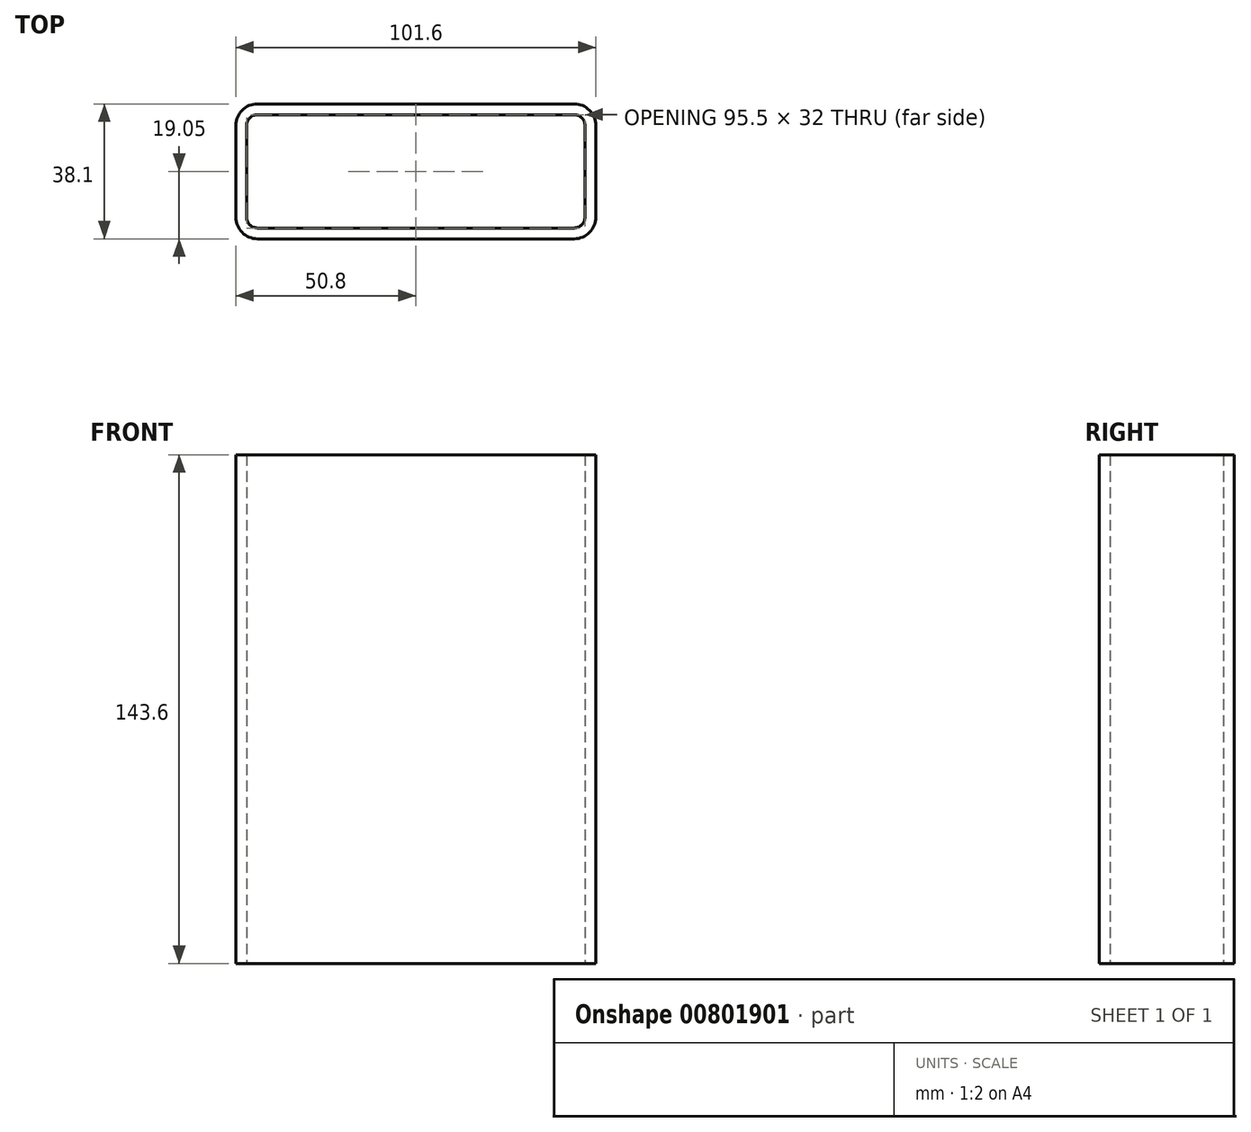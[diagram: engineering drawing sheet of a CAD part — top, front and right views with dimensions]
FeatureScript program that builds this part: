
annotation { "Feature Type Name" : "Feature", "Feature Type Description" : "" }
export const myFeature = defineFeature(function(context is Context, id is Id, definition is map)
    precondition{}
    {
        {
            var Q0;
            Q0=qCreatedBy(makeId("Top.planeOp"),FACE);
            var sketch = newSketch(context, id + "F0", { "sketchPlane" : qUnion([Q0])});
            skLineSegment(sketch, "E0.bottom", {"start": v(6.1, 0) * mm, "end": v(95.5, 0) * mm});
            skLineSegment(sketch, "E0.top", {"start": v(6.1, 38.1) * mm, "end": v(95.5, 38.1) * mm});
            skLineSegment(sketch, "E0.left", {"start": v(0, 6.1) * mm, "end": v(0, 32) * mm});
            skLineSegment(sketch, "E0.right", {"start": v(101.6, 6.1) * mm, "end": v(101.6, 32) * mm});
            skLineSegment(sketch, "E1.bottom", {"start": v(6.1, 35.05) * mm, "end": v(95.5, 35.05) * mm});
            skLineSegment(sketch, "E1.top", {"start": v(6.1, 3.05) * mm, "end": v(95.5, 3.05) * mm});
            skLineSegment(sketch, "E1.left", {"start": v(3.05, 32) * mm, "end": v(3.05, 6.1) * mm});
            skLineSegment(sketch, "E1.right", {"start": v(98.55, 32) * mm, "end": v(98.55, 6.1) * mm});
            skPoint(sketch, "E2.visualSharp", {"position": v(3.05, 35.05) * mm});
            skArc(sketch, "E2.filletArc", {"start": v(6.1, 35.05) * mm, "mid": v(3.94, 34.16) * mm, "end": v(3.05, 32) * mm});
            skPoint(sketch, "E3.visualSharp", {"position": v(98.55, 35.05) * mm});
            skArc(sketch, "E3.filletArc", {"start": v(98.55, 32) * mm, "mid": v(97.66, 34.16) * mm, "end": v(95.5, 35.05) * mm});
            skPoint(sketch, "E4.visualSharp", {"position": v(98.55, 3.05) * mm});
            skArc(sketch, "E4.filletArc", {"start": v(95.5, 3.05) * mm, "mid": v(97.66, 3.94) * mm, "end": v(98.55, 6.1) * mm});
            skPoint(sketch, "E5.visualSharp", {"position": v(3.05, 3.05) * mm});
            skArc(sketch, "E5.filletArc", {"start": v(3.05, 6.1) * mm, "mid": v(3.94, 3.94) * mm, "end": v(6.1, 3.05) * mm});
            skPoint(sketch, "E6.visualSharp", {"position": v(0, 38.1) * mm});
            skArc(sketch, "E6.filletArc", {"start": v(6.1, 38.1) * mm, "mid": v(1.79, 36.31) * mm, "end": v(0, 32) * mm});
            skPoint(sketch, "E7.visualSharp", {"position": v(101.6, 38.1) * mm});
            skArc(sketch, "E7.filletArc", {"start": v(101.6, 32) * mm, "mid": v(99.81, 36.31) * mm, "end": v(95.5, 38.1) * mm});
            skPoint(sketch, "E8.visualSharp", {"position": v(101.6, 0) * mm});
            skArc(sketch, "E8.filletArc", {"start": v(95.5, 0) * mm, "mid": v(99.81, 1.79) * mm, "end": v(101.6, 6.1) * mm});
            skPoint(sketch, "E9.visualSharp", {"position": v(0, 0) * mm});
            skArc(sketch, "E9.filletArc", {"start": v(0, 6.1) * mm, "mid": v(1.79, 1.79) * mm, "end": v(6.1, 0) * mm});
            skSolve(sketch);
        }
        {
            var Q0;
            Q0=qSketchRegion(id+"F0",true);
            extrude(context, id + "F1", {"entities" : qUnion([Q0]), "offsetDistance" : 25 * mm, "depth" : 143.6 * mm});
        }
    });
